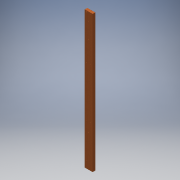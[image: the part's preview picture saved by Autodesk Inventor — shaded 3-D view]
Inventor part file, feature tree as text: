
AUTODESK INVENTOR PART (.ipt)
format: ipt  version: 2016 (Build 200138000, 138)  size: 131,072 bytes
history: native  units: in
note: dims shown in document units (in); Inventor stores cm internally (conversion verified against a paired STEP export)
features: sketch x4, hole x3, extrude x1
ambient origin geometry x8: Origin, YZ Plane, XZ Plane, XY Plane, X Axis, Y Axis, Z Axis, Center Point
bodies: Solid1 (feature_tree)
feature tree (8):
  extrude  "Extrusion1"  Depth=1.4961in
  hole  "rimArm"  [1 undecoded]
  hole  "screenArm"  [1 undecoded]
  hole  "poleAttach"  [1 undecoded]
  sketch  "Sketch1"  dims[d0=4.4882in d1=1.4961in]
  sketch  "Sketch3"  dims[d2=78.7402in d3=0.0in d28=4.0in]
  sketch  "Sketch4"  dims[d29=1.122in d30=0.7874in d32=2.2441in d33=0.7874in d35=20.0in]
  sketch  "Sketch5"  dims[d38=0.25in d39=0.75in d40=0.375in d41=0.25in d42=0.5635in d43=1.0in d44=0.8108in d45=0.75in d46=0.7874in d48=2.2441in d49=0.7874in d51=25.0in d54=0.266in d55=0.75in d56=0.762in d57=0.25in d58=0.5635in d59=1.0in d60=0.8108in d61=5.0in d62=18.5in d63=0.397in d64=0.75in d65=0.762in d66=0.25in d67=0.5635in d68=1.0in d69=0.8108in d70=65.0in d71=1.122in d72=2.2441in d73=2.2441in d74=2.2441in]
note: 3 required parameter values undecoded (feature->parameter linkage not recoverable at this tier; creation-order binding heuristic only, values carry confidence <= 0.55)
